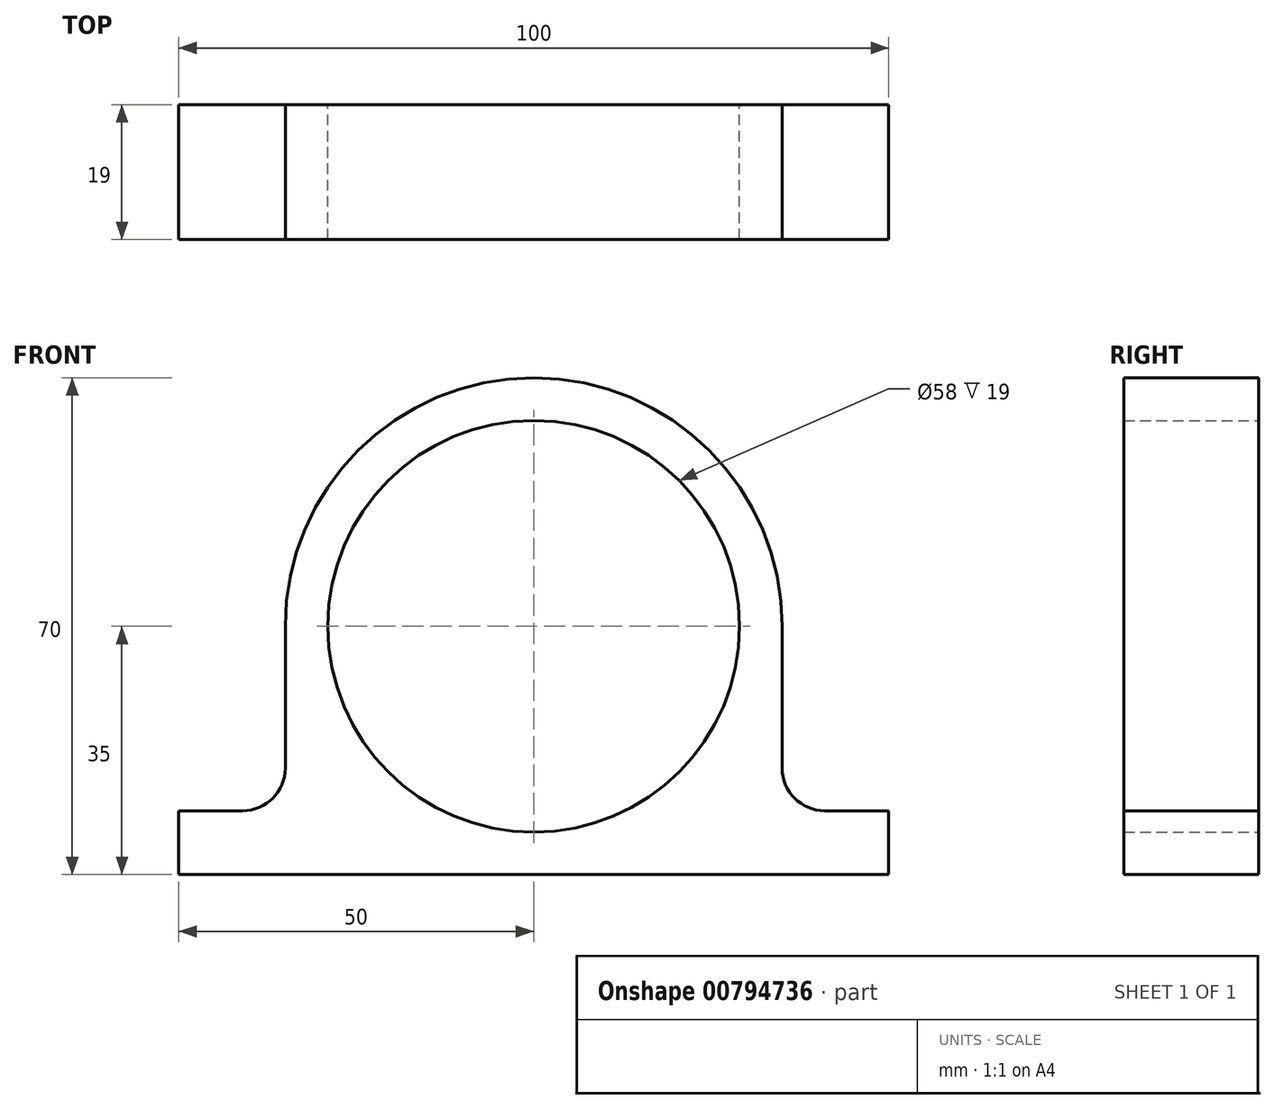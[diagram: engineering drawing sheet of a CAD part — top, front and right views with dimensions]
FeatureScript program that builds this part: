
annotation { "Feature Type Name" : "Feature", "Feature Type Description" : "" }
export const myFeature = defineFeature(function(context is Context, id is Id, definition is map)
    precondition{}
    {
        {
            var Q0;
            Q0=qCreatedBy(makeId("Front.planeOp"),FACE);
            var sketch = newSketch(context, id + "F0", { "sketchPlane" : qUnion([Q0])});
            skCircle(sketch, "E0", {"center": v(0, 0) * mm, "radius": 29 * mm});
            skArc(sketch, "E1", {"start": v(35, 0) * mm, "mid": v(0, 35) * mm, "end": v(-35, 0) * mm});
            skLineSegment(sketch, "E2", {"start": v(0, -35) * mm, "end": v(50, -35) * mm});
            skLineSegment(sketch, "E3", {"start": v(50, -35) * mm, "end": v(50, -26) * mm});
            skLineSegment(sketch, "E4", {"start": v(0, 0) * mm, "end": v(35, 0) * mm, "construction": true});
            skLineSegment(sketch, "E5", {"start": v(35, 0) * mm, "end": v(35, -26) * mm});
            skLineSegment(sketch, "E6", {"start": v(35, -26) * mm, "end": v(50, -26) * mm});
            skLineSegment(sketch, "E7", {"start": v(0, 0) * mm, "end": v(0, -35) * mm, "construction": true});
            skLineSegment(sketch, "E8.MirrorCS", {"start": v(-35, 0) * mm, "end": v(-35, -26) * mm});
            skLineSegment(sketch, "E9.MirrorCS", {"start": v(-35, -26) * mm, "end": v(-50, -26) * mm});
            skLineSegment(sketch, "E10.MirrorCS", {"start": v(-50, -35) * mm, "end": v(-50, -26) * mm});
            skLineSegment(sketch, "E11.MirrorCS", {"start": v(0, -35) * mm, "end": v(-50, -35) * mm});
            skSolve(sketch);
        }
        {
            var Q0;
            Q0=makeQuery(id+"F0.imprint","IMPRINT",FACE,{"disambiguationData":[TD([[makeQuery(id+"F0.imprint","IMPRINT",EDGE,{"derivedFrom":sQuery(id+"F0.wireOp",EDGE,"E0")}),-1.0]])]});
            extrude(context, id + "F1", {"entities" : qUnion([Q0]), "depth" : 19 * mm, "offsetDistance" : 25 * mm});
        }
        {
            var Q0;
            Q0=makeQuery(id+"F1.opExtrude","SWEPT_EDGE",EDGE,{"disambiguationData":[OSD([sQuery(id+"F0.wireOp",EDGE,"E8.MirrorCS"),sQuery(id+"F0.wireOp",EDGE,"E9.MirrorCS")])]});
            var Q1;
            Q1=makeQuery(id+"F1.opExtrude","SWEPT_EDGE",EDGE,{"disambiguationData":[OSD([sQuery(id+"F0.wireOp",EDGE,"E5"),sQuery(id+"F0.wireOp",EDGE,"E6")])]});
            fillet(context, id + "F2", {"entities" : qUnion([Q0, Q1]), "radius" : 6 * mm, "tangentPropagation" : true, "allowEdgeOverflow" : false});
        }
    });
